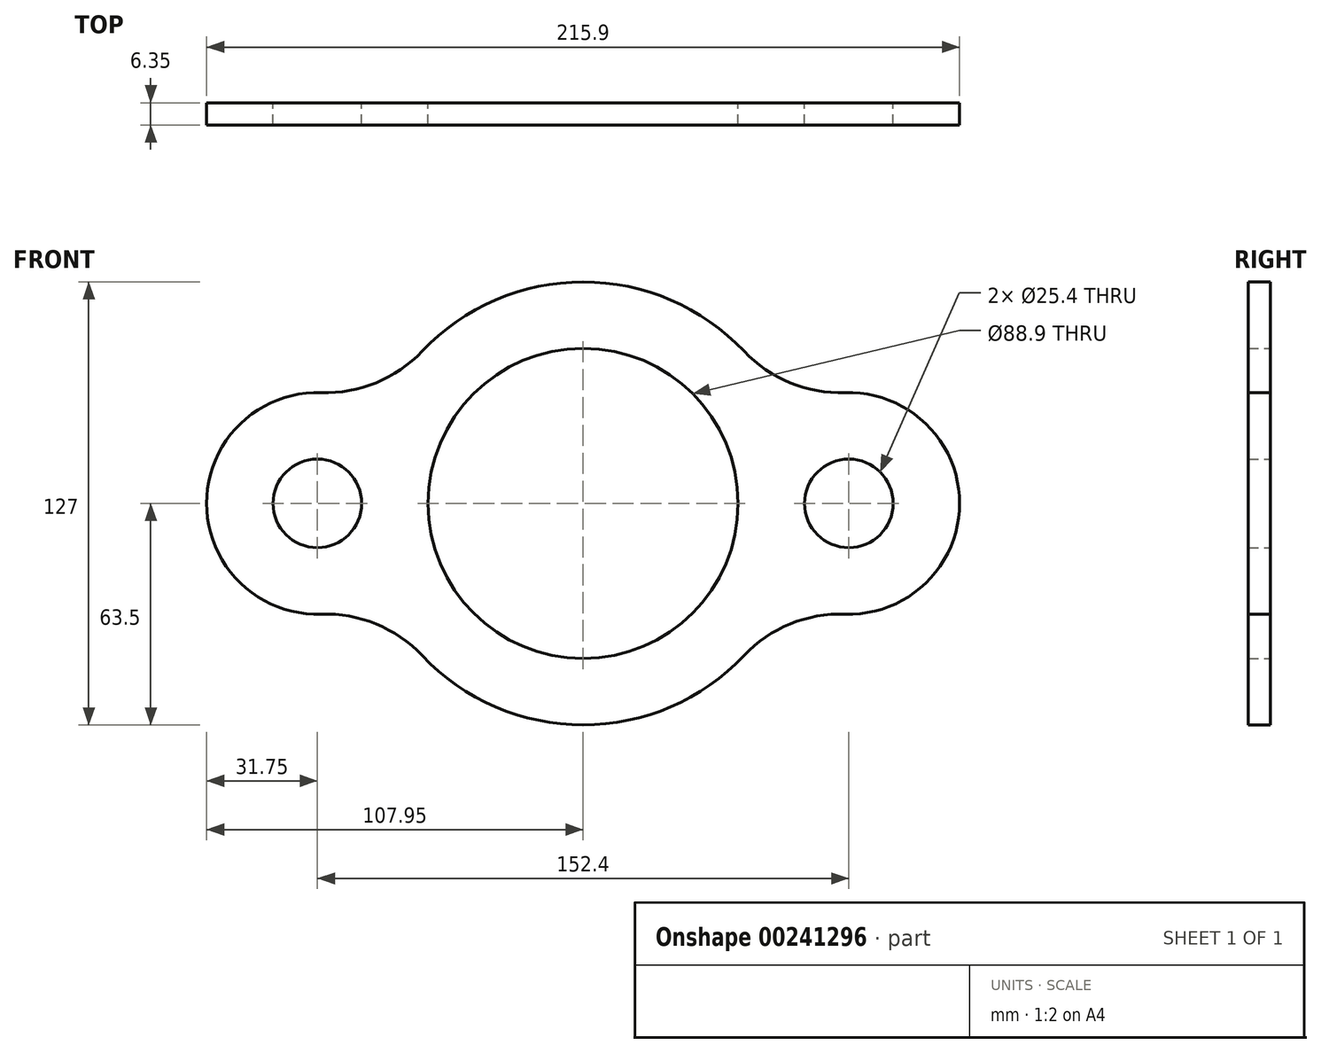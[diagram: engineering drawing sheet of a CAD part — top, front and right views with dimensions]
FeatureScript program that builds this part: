
annotation { "Feature Type Name" : "Feature", "Feature Type Description" : "" }
export const myFeature = defineFeature(function(context is Context, id is Id, definition is map)
    precondition{}
    {
        {
            var Q0;
            Q0=qCreatedBy(makeId("Front.planeOp"),FACE);
            var sketch = newSketch(context, id + "F0", { "sketchPlane" : qUnion([Q0])});
            skArc(sketch, "E0", {"start": v(-46.14, -43.63) * mm, "mid": v(0, -63.5) * mm, "end": v(46.14, -43.63) * mm});
            skCircle(sketch, "E1", {"center": v(0, 0) * mm, "radius": 44.45 * mm});
            skCircle(sketch, "E2", {"center": v(76.2, 0) * mm, "radius": 12.7 * mm});
            skArc(sketch, "E3", {"start": v(75.12, -31.73) * mm, "mid": v(107.95, 0) * mm, "end": v(75.12, 31.73) * mm});
            skCircle(sketch, "E4", {"center": v(-76.2, 0) * mm, "radius": 12.7 * mm});
            skArc(sketch, "E5", {"start": v(-75.12, 31.73) * mm, "mid": v(-107.95, 0) * mm, "end": v(-75.12, -31.73) * mm});
            skArc(sketch, "E6.trimOffspring", {"start": v(46.14, 43.63) * mm, "mid": v(0, 63.5) * mm, "end": v(-46.14, 43.63) * mm});
            skPoint(sketch, "E7.visualSharp", {"position": v(-57.94, 25.98) * mm});
            skArc(sketch, "E7.filletArc", {"start": v(-75.12, 31.73) * mm, "mid": v(-59.35, 34.56) * mm, "end": v(-46.14, 43.63) * mm});
            skPoint(sketch, "E8.visualSharp", {"position": v(-57.94, -25.98) * mm});
            skArc(sketch, "E8.filletArc", {"start": v(-46.14, -43.63) * mm, "mid": v(-59.35, -34.56) * mm, "end": v(-75.12, -31.73) * mm});
            skPoint(sketch, "E9.visualSharp", {"position": v(57.94, -25.98) * mm});
            skArc(sketch, "E9.filletArc", {"start": v(75.12, -31.73) * mm, "mid": v(59.35, -34.56) * mm, "end": v(46.14, -43.63) * mm});
            skPoint(sketch, "E10.visualSharp", {"position": v(57.94, 25.98) * mm});
            skArc(sketch, "E10.filletArc", {"start": v(46.14, 43.63) * mm, "mid": v(59.35, 34.56) * mm, "end": v(75.12, 31.73) * mm});
            skSolve(sketch);
        }
        {
            var Q0;
            Q0 = qSketchRegion(id + "F0", true);
            extrude(context, id + "F1", {"entities" : qUnion([Q0]), "depth" : 6.35 * mm});
        }
    });
